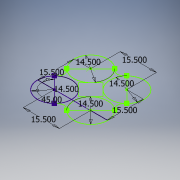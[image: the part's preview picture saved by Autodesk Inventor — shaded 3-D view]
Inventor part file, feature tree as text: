
AUTODESK INVENTOR PART (.ipt)
format: ipt  version: 2017 (Build 210142000, 142)  size: 103,424 bytes
history: native  units: in
note: dims shown in document units (in); Inventor stores cm internally (conversion verified against a paired STEP export)
features: sketch x1
ambient origin geometry x8: Origin, YZ Plane, XZ Plane, XY Plane, X Axis, Y Axis, Z Axis, Center Point
feature tree (1):
  sketch  "Sketch1"  dims[d0=14.5in d1=15.5in d2=14.5in d3=45.0deg d4=15.5in d5=14.5in d6=14.5in d7=15.5in d8=15.5in]
